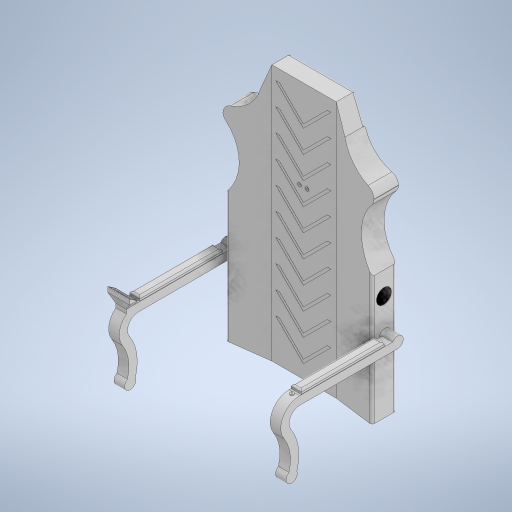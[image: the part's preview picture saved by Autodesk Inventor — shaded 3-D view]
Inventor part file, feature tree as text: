
AUTODESK INVENTOR PART (.ipt)
format: ipt  version: 2023 (Build 270158030, 158C)  size: 860,672 bytes
history: native  units: in
note: dims shown in document units (in); Inventor stores cm internally (conversion verified against a paired STEP export)
features: sketch x25, extrude x21, plane x4, mirror x3, pattern_linear x2, fillet x2, projected_geometry x2, sweep x1, loft x1, shell x1
ambient origin geometry x8: Origin, YZ Plane, XZ Plane, XY Plane, X Axis, Y Axis, Z Axis, Center Point
bodies: Solid1 (feature_tree)
feature tree (62):
  extrude  "Extrusion1"  Depth=34.0in
  extrude  "Extrusion2"  Depth=2.0in
  extrude  "Extrusion3"  Depth=1.95in
  plane  "Work Plane1"
  mirror  "Mirror2"
  extrude  "Extrusion4"  Depth=0.25in
  extrude  "Extrusion5"  Depth=4.188in
  extrude  "Extrusion6"  Depth=0.25in
  pattern_linear  "Rectangular Pattern1"  Spacing1=0.5in  [1 undecoded]
  extrude  "Extrusion8"  Depth=0.5in
  plane  "Work Plane2"
  extrude  "Extrusion9"  Depth=0.1in
  sketch  "Sketch11"  dims[d16=17.0in]
  plane  "Work Plane3"
  sweep  "Sweep1"
  extrude  "Extrusion10"  Depth=0.1in
  extrude  "Extrusion11"  Depth=0.1in
  fillet  "Fillet1"  Radius=1.558in
  mirror  "Mirror4"
  extrude  "Extrusion12"  Depth=0.1in TaperAngle=0.0deg
  extrude  "Extrusion13"  Depth=0.1in
  extrude  "Extrusion14"  Depth=0.1in
  pattern_linear  "Rectangular Pattern2"  Spacing1=1.5in  [1 undecoded]
  extrude  "Extrusion15"  Depth=0.1in
  fillet  "Fillet2"  Radius=1.7in
  extrude  "Extrusion16"  Depth=0.1in
  extrude  "Extrusion17"  Depth=1.1in
  sketch  "Sketch22"  dims[d27=6.1379in]
  plane  "Work Plane5"
  loft  "Loft1"
  extrude  "Extrusion18"  Depth=1.0in TaperAngle=0.0deg
  extrude  "Extrusion19"  Depth=1.1in
  extrude  "Extrusion20"  [1 undecoded]
  extrude  "Extrusion21"  Depth=0.1in
  extrude  "Extrusion22"  Depth=0.1in
  mirror  "Mirror5"
  shell  "Shell1"  Thickness=4.214in
  sketch  "Sketch1"  dims[d0=20.0in d1=34.0in]
  sketch  "Sketch2"  dims[d2=2.5in d3=0.0in d4=2.0in]
  sketch  "Sketch3"  dims[d5=1.95in d6=1.95in]
  sketch  "Sketch4"  dims[d7=0.25in d8=0.25in]
  projected_geometry  "Projected Loop1"
  sketch  "Sketch5"  dims[d9=4.188in d10=4.188in]
  sketch  "Sketch7"  dims[d11=0.25in d12=0.25in]
  sketch  "Sketch9"  dims[d13=1.5in d14=0.0in]
  sketch  "Sketch10"  dims[d15=0.3in]
  sketch  "Sketch12"  dims[d17=5.0in]
  sketch  "Sketch13"  dims[d18=45.0deg]
  sketch  "Sketch14"  dims[d19=0.4679in]
  sketch  "Sketch15"  dims[d20=4.8242in]
  sketch  "Sketch16"  dims[d21=1.1506in]
  sketch  "Sketch17"  dims[d22=6.1379in]
  sketch  "Sketch19"  dims[d23=8.2712in]
  sketch  "Sketch20"  dims[d24=2.5in d25=0.0in]
  sketch  "Sketch21"  dims[d26=10.0in]
  sketch  "Sketch23"  dims[d28=1.3269in]
  sketch  "Sketch24"  dims[d29=6.1379in]
  sketch  "Sketch25"  dims[d30=0.75in d31=0.0in]
  projected_geometry  "Projected Loop2"
  sketch  "Sketch26"  dims[d32=34.0in d33=0.0in]
  sketch  "Sketch27"  dims[d34=0.5in]
  sketch  "Sketch28"  dims[d35=135.0deg d36=0.5in d37=0.5in d38=0.698in d39=45.0deg d40=4.7206in d41=0.6081in d42=1.558in d43=0.01in d44=0.0in d45=3.937in d47=3.0in d56=1.5in d57=1.5in d58=9.5in d59=1.7in d60=0.0in d61=1.5in d62=1.1in d63=1.4in d65=1.0in d66=0.0in d67=1.1in d68=-0.7in d70=1.9454in d71=5.5746in d73=4.214in d75=12.0in d76=0.0in d77=0.0in d79=13.0432in d80=1.5in d81=1.0in d82=0.0in d83=0.05in d84=0.05in d85=1.1in d86=0.25in d87=0.5in d88=0.0in d89=0.25in d90=6.25in d91=8.0in d92=6.45in d94=7.9in d95=1.0in d96=0.0in d97=0.75in d98=0.5in d99=0.25in d100=0.0in d101=0.25in d102=0.75in d103=0.0in d104=1.9685in d106=1.5in d107=0.25in d108=2.0in d109=0.25in d110=2.5in d111=0.75in d112=0.0in d116=0.5in d117=0.525in d118=1.0in d119=0.3in d120=7.2in d121=0.5in d122=0.5in d123=0.5in d124=0.5in d125=0.75in d126=0.0in d127=1.2in d128=0.35in d129=0.75in d130=0.0in d131=1.0in d132=0.5in d134=0.75in d135=0.75in d136=1.0in d137=0.0in d138=90.0deg d139=0.0in d140=90.0deg d141=0.2405in d142=0.75in d143=2.15in d144=0.0in d145=0.0in d146=0.1in d147=0.1in d148=0.0in d149=0.5in d150=0.1in d151=0.05in d152=0.0in d153=0.0in d154=0.1in d155=0.05in d156=0.0in d157=2.0in d158=3.0in d160=1.55in d161=0.05in d162=0.0in d163=0.1in]
note: 3 required parameter values undecoded (feature->parameter linkage not recoverable at this tier; creation-order binding heuristic only, values carry confidence <= 0.55)
